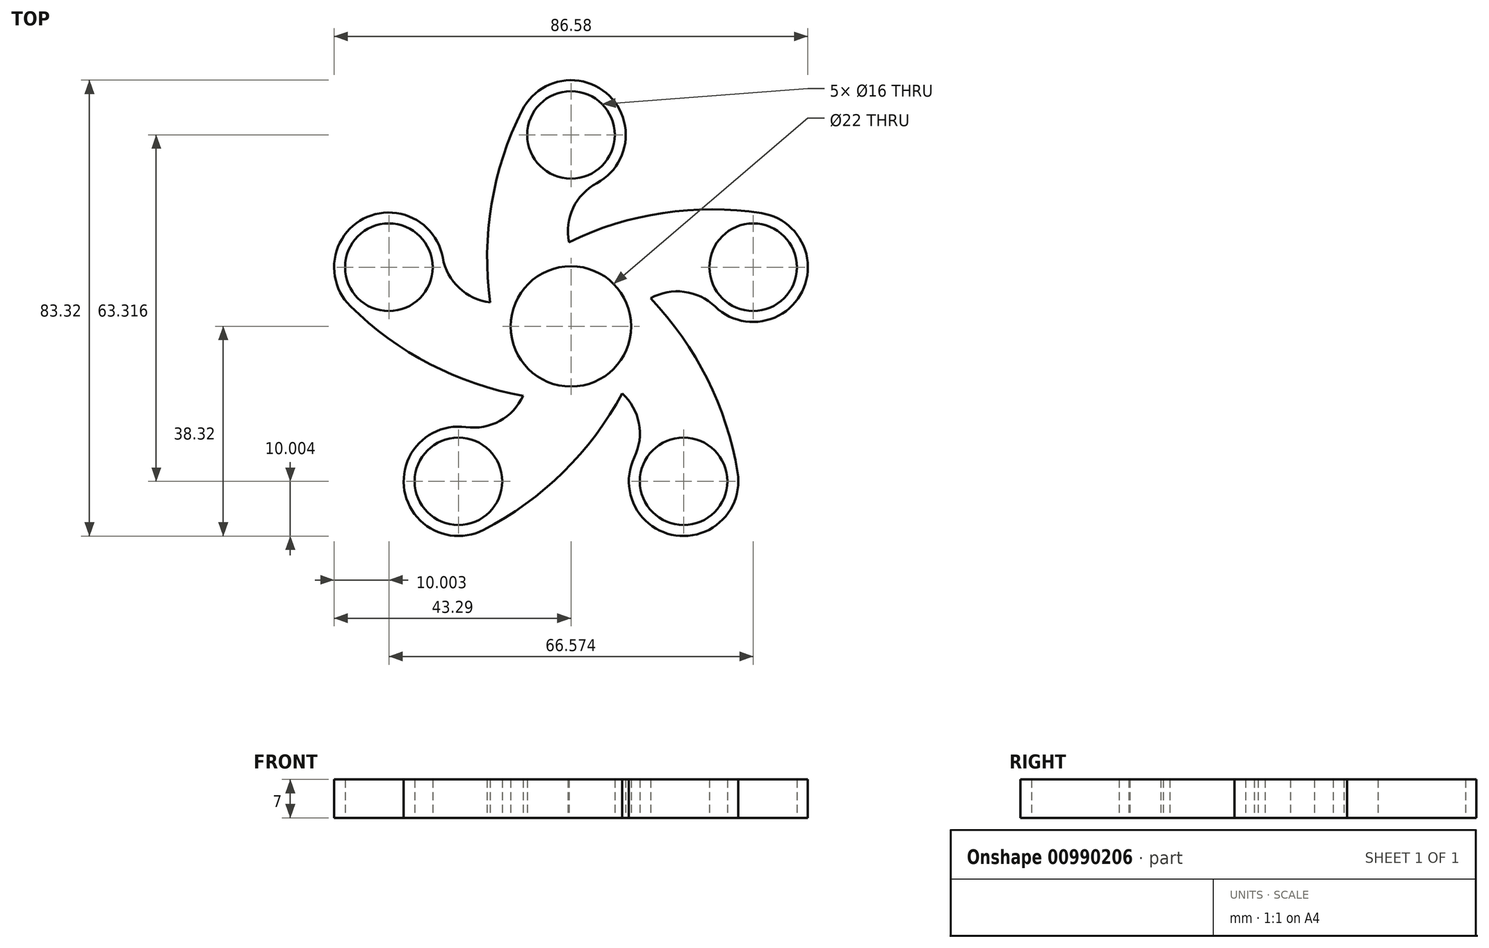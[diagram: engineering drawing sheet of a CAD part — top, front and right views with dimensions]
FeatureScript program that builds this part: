
annotation { "Feature Type Name" : "Feature", "Feature Type Description" : "" }
export const myFeature = defineFeature(function(context is Context, id is Id, definition is map)
    precondition{}
    {
        {
            assignVariable(context, id + "F0", {"name" : "number_of_arms", "anyValue" : 5});
        }
        {
            var Q0;
            Q0=qCreatedBy(makeId("Top.planeOp"),FACE);
            var sketch = newSketch(context, id + "F1", { "sketchPlane" : qUnion([Q0])});
            skCircle(sketch, "E0", {"center": v(0, 0) * mm, "radius": 11 * mm});
            skCircle(sketch, "E1", {"center": v(0, 0) * mm, "radius": 14 * mm});
            skCircle(sketch, "E2", {"center": v(0, 35) * mm, "radius": 8 * mm});
            skCircle(sketch, "E3", {"center": v(0, 35) * mm, "radius": 10 * mm});
            skArc(sketch, "E4", {"start": v(-8.93, 39.5) * mm, "mid": v(-14.84, 20.18) * mm, "end": v(-14, 0) * mm});
            skArc(sketch, "E5", {"start": v(4.7, 26.18) * mm, "mid": v(0.1, 20.96) * mm, "end": v(0, 14) * mm});
            skSolve(sketch);
        }
        {
            var Q0;
            Q0=qSketchRegion(id+"F1",true);
            extrude(context, id + "F2", {"entities" : qUnion([Q0]), "depth" : 7 * mm, "offsetDistance" : 25 * mm});
        }
        {
            var Q0;
            Q0=makeQuery(id+"F2.opExtrude","SWEPT_BODY",BODY,{"disambiguationData":[OSD([sQuery(id+"F1.wireOp",EDGE,"E0"),sQuery(id+"F1.wireOp",EDGE,"E1"),sQuery(id+"F1.wireOp",EDGE,"E2"),sQuery(id+"F1.wireOp",EDGE,"E3"),sQuery(id+"F1.wireOp",EDGE,"E4"),sQuery(id+"F1.wireOp",EDGE,"E5")])]});
            var Q1;
            Q1=makeQuery(id+"F2.opExtrude","CAP_EDGE",EDGE,{"disambiguationData":[OSD([sQuery(id+"F1.wireOp",EDGE,"E0")])],"isStart":false});
            circularPattern(context, id + "F3", {"operationType" : NewBodyOperationType.ADD, "entities" : qUnion([Q0]), "axis" : qUnion([Q1]), "angle" : 360 * degree, "instanceCount" : getVariable(context, 'number_of_arms'), "equalSpace" : true});
        }
    });
